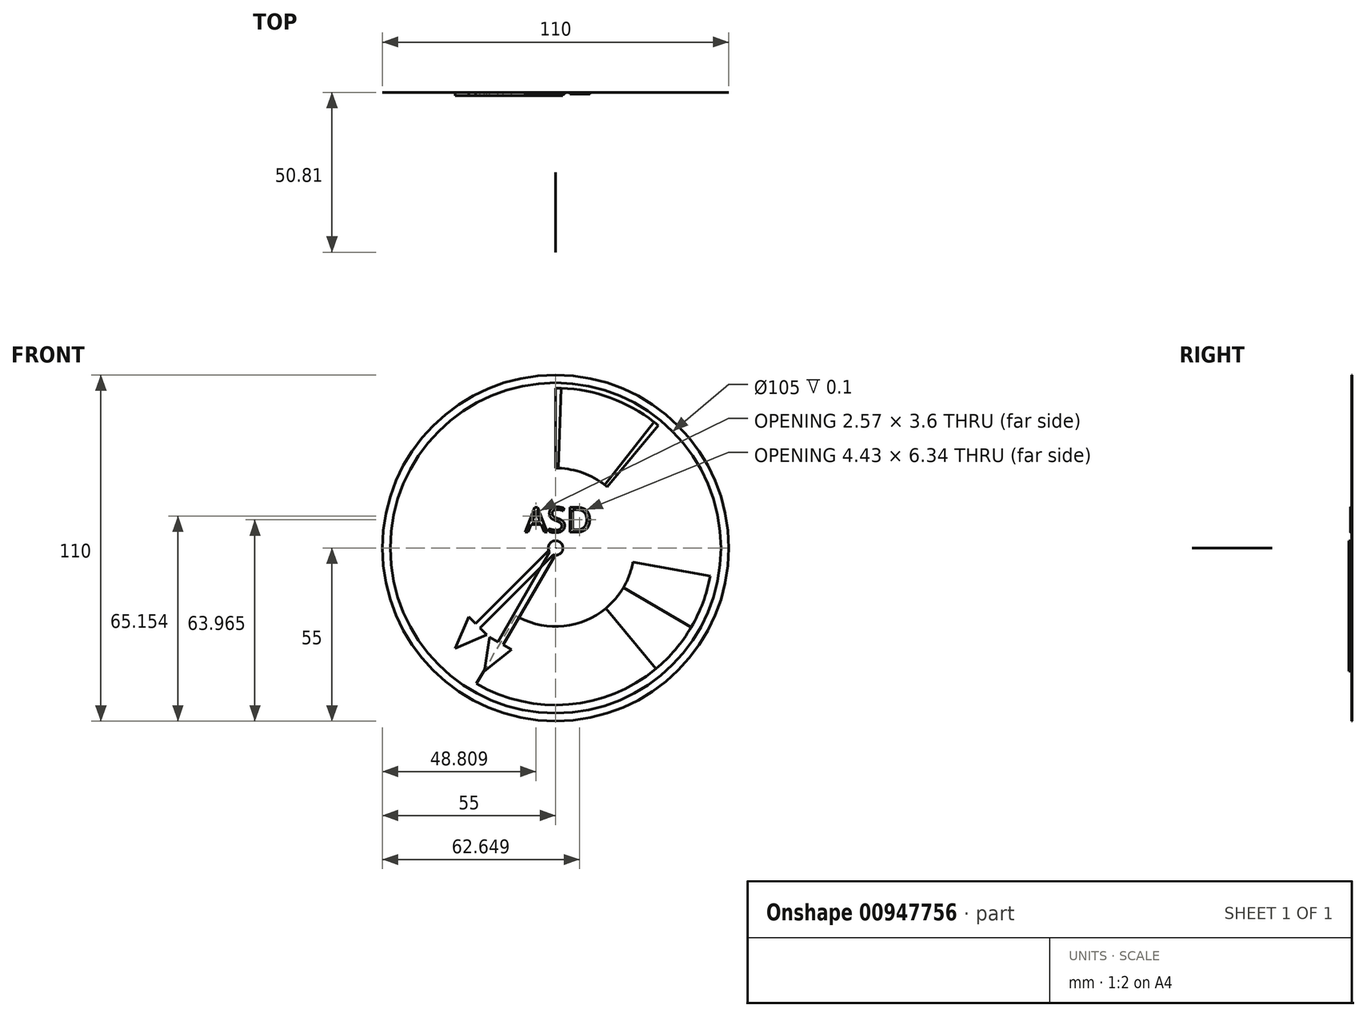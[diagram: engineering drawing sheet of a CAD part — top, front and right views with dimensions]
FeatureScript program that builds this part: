
annotation { "Feature Type Name" : "Feature", "Feature Type Description" : "" }
export const myFeature = defineFeature(function(context is Context, id is Id, definition is map)
    precondition{}
    {
        {
            var Q0;
            Q0=qCreatedBy(makeId("Right.planeOp"),FACE);
            var sketch = newSketch(context, id + "F0", { "sketchPlane" : qUnion([Q0])});
            skLineSegment(sketch, "E0", {"start": v(0, 0) * mm, "end": v(-116.06, 0) * mm, "construction": true});
            skSolve(sketch);
        }
        {
            var Q0;
            Q0=qCreatedBy(makeId("Right.planeOp"),FACE);
            var Q1;
            Q1=sQuery(id+"F0.wireOp",EDGE,"E0");
            cPlane(context, id + "F1", {"entities" : qUnion([Q0, Q1]), "cplaneType" : CPlaneType.LINE_ANGLE, "offset" : 25 * mm, "angle" : 135 * degree, "width" : 150 * mm, "height" : 150 * mm});
        }
        {
            var Q0;
            Q0=qCreatedBy(id+"F1.planeOp",FACE);
            var sketch = newSketch(context, id + "F2", { "sketchPlane" : qUnion([Q0])});
            skLineSegment(sketch, "E1.bottom", {"start": v(-25.4, 0) * mm, "end": v(-50.8, 0) * mm});
            skLineSegment(sketch, "E1.top", {"start": v(-25.4, 0) * mm, "end": v(-50.8, 0) * mm});
            skLineSegment(sketch, "E1.left", {"start": v(-25.4, 0) * mm, "end": v(-25.4, 0) * mm});
            skLineSegment(sketch, "E1.right", {"start": v(-50.8, 0) * mm, "end": v(-50.8, 0) * mm});
            skSolve(sketch);
        }
        {
            var Q0;
            Q0=qSketchRegion(id+"F2",true);
            var Q1;
            Q1=sQuery(id+"F0.wireOp",EDGE,"E0");
            revolve(context, id + "F3", {"surfaceOperationType" : NewSurfaceOperationType.NEW, "entities" : qUnion([Q0]), "axis" : qUnion([Q1]), "revolveType" : RevolveType.ONE_DIRECTION, "oppositeDirection" : true, "angle" : 135 * degree});
        }
        {
            var Q0;
            Q0=qCreatedBy(makeId("Right.planeOp"),FACE);
            var sketch = newSketch(context, id + "F4", { "sketchPlane" : qUnion([Q0])});
            skLineSegment(sketch, "E2.bottom", {"start": v(-0.01, 50.8) * mm, "end": v(0, 50.8) * mm});
            skLineSegment(sketch, "E2.top", {"start": v(0, 25.4) * mm, "end": v(0, 25.4) * mm});
            skLineSegment(sketch, "E2.left", {"start": v(-0.01, 50.8) * mm, "end": v(0, 25.4) * mm});
            skLineSegment(sketch, "E2.right", {"start": v(0, 50.8) * mm, "end": v(0, 25.4) * mm});
            skSolve(sketch);
        }
        {
            var Q0;
            Q0=qSketchRegion(id+"F4",true);
            var Q1;
            Q1=sQuery(id+"F0.wireOp",EDGE,"E0");
            revolve(context, id + "F5", {"surfaceOperationType" : NewSurfaceOperationType.NEW, "entities" : qUnion([Q0]), "axis" : qUnion([Q1]), "revolveType" : RevolveType.ONE_DIRECTION, "oppositeDirection" : true, "angle" : 2 * degree});
        }
        {
            var Q0;
            Q0=qCreatedBy(makeId("Right.planeOp"),FACE);
            var Q1;
            Q1=sQuery(id+"F0.wireOp",EDGE,"E0");
            cPlane(context, id + "F6", {"entities" : qUnion([Q0, Q1]), "cplaneType" : CPlaneType.LINE_ANGLE, "offset" : 25 * mm, "angle" : 2 * degree, "oppositeDirection" : true, "width" : 150 * mm, "height" : 150 * mm});
        }
        {
            var Q0;
            Q0=qCreatedBy(id+"F6.planeOp",FACE);
            var sketch = newSketch(context, id + "F7", { "sketchPlane" : qUnion([Q0])});
            skLineSegment(sketch, "E3.bottom", {"start": v(0, 50.8) * mm, "end": v(0, 50.8) * mm});
            skLineSegment(sketch, "E3.top", {"start": v(0, 25.4) * mm, "end": v(0, 25.4) * mm});
            skLineSegment(sketch, "E3.left", {"start": v(0, 50.8) * mm, "end": v(0, 25.4) * mm});
            skLineSegment(sketch, "E3.right", {"start": v(0, 50.8) * mm, "end": v(0, 25.4) * mm});
            skSolve(sketch);
        }
        {
            var Q0;
            Q0=qSketchRegion(id+"F7",true);
            var Q1;
            Q1=sQuery(id+"F0.wireOp",EDGE,"E0");
            revolve(context, id + "F8", {"surfaceOperationType" : NewSurfaceOperationType.NEW, "entities" : qUnion([Q0]), "axis" : qUnion([Q1]), "revolveType" : RevolveType.ONE_DIRECTION, "oppositeDirection" : true, "angle" : 36 * degree});
        }
        {
            var Q0;
            Q0=qCreatedBy(makeId("Front.planeOp"),FACE);
            var sketch = newSketch(context, id + "F9", { "sketchPlane" : qUnion([Q0])});
            skLineSegment(sketch, "E4.bottom", {"start": v(-0.77, -2.19) * mm, "end": v(-24.04, -25.46) * mm});
            skLineSegment(sketch, "E4.top", {"start": v(-2.19, -0.77) * mm, "end": v(-25.46, -24.04) * mm});
            skPoint(sketch, "E4.middle", {"position": v(0, 0) * mm});
            skLineSegment(sketch, "E5", {"start": v(0, 0) * mm, "end": v(0, 10.99) * mm, "construction": true});
            skPoint(sketch, "E6", {"position": v(-24.75, -24.75) * mm});
            skCircle(sketch, "E7", {"center": v(-24.75, -24.75) * mm, "radius": 10.19 * mm, "construction": true});
            skLineSegment(sketch, "E8", {"start": v(-24.04, -25.46) * mm, "end": v(-21.92, -27.58) * mm});
            skLineSegment(sketch, "E9", {"start": v(-25.46, -24.04) * mm, "end": v(-27.58, -21.92) * mm});
            skLineSegment(sketch, "E10", {"start": v(-24.75, -24.75) * mm, "end": v(-31.95, -31.95) * mm, "construction": true});
            skLineSegment(sketch, "E11", {"start": v(-31.95, -31.95) * mm, "end": v(-27.58, -21.92) * mm});
            skLineSegment(sketch, "E12", {"start": v(-21.92, -27.58) * mm, "end": v(-31.95, -31.95) * mm});
            skArc(sketch, "E13", {"start": v(-0.77, -2.19) * mm, "mid": v(1.64, 1.64) * mm, "end": v(-2.19, -0.77) * mm});
            skPoint(sketch, "E14.orphan", {"position": v(-0.7, 0.7) * mm});
            skPoint(sketch, "E15.end.orphan", {"position": v(0.7, -0.7) * mm});
            skSolve(sketch);
        }
        {
            var Q0;
            Q0=qSketchRegion(id+"F9",true);
            extrude(context, id + "F10", {"entities" : qUnion([Q0]), "depth" : 1 * mm, "offsetDistance" : 25 * mm});
        }
        {
            var Q0;
            Q0=qCreatedBy(makeId("Front.planeOp"),FACE);
            var sketch = newSketch(context, id + "F11", { "sketchPlane" : qUnion([Q0])});
            skCircle(sketch, "E16", {"center": v(0, 0) * mm, "radius": 52.5 * mm});
            skCircle(sketch, "E17", {"center": v(0, 0) * mm, "radius": 55 * mm});
            skSolve(sketch);
        }
        {
            var Q0;
            Q0=qSketchRegion(id+"F11",true);
            extrude(context, id + "F12", {"entities" : qUnion([Q0]), "depth" : .1 * mm, "offsetDistance" : 25 * mm});
        }
        {
            var Q0;
            Q0=qCreatedBy(makeId("Front.planeOp"),FACE);
            var sketch = newSketch(context, id + "F13", { "sketchPlane" : qUnion([Q0])});
            skPoint(sketch, "E18.middle", {"position": v(68.26, -76.77) * mm});
            skText(sketch, "E19", { "text": "SPEED", "fontName": "OpenSans-Bold.ttf"});
            skLineSegment(sketch, "E20", {"start": v(0, 0) * mm, "end": v(0, -24.7) * mm, "construction": true});
            const initialGuessF13  = {"E19": [-0.015, -0.03702, 1, 0, 0.007]};
            skSetInitialGuess(sketch, initialGuessF13);
            skSolve(sketch);
        }
        {
            var Q0;
            Q0 = qSketchRegion(id + "F13", true);
            extrude(context, id + "F14", {"entities" : qUnion([Q0]), "depth" : .1 * mm, "offsetDistance" : 25 * mm});
        }
        {
            var Q0;
            Q0=qCreatedBy(makeId("Front.planeOp"),FACE);
            var sketch = newSketch(context, id + "F15", { "sketchPlane" : qUnion([Q0])});
            skLineSegment(sketch, "E21", {"start": v(3.53, 25.15) * mm, "end": v(7.07, 50.3) * mm});
            skLineSegment(sketch, "E22", {"start": v(0, 0) * mm, "end": v(0, 18.46) * mm, "construction": true});
            skArc(sketch, "E23", {"start": v(3.53, 25.15) * mm, "mid": v(3.97, 25.09) * mm, "end": v(4.41, 25.01) * mm});
            skArc(sketch, "E24", {"start": v(7.07, 50.3) * mm, "mid": v(7.95, 50.17) * mm, "end": v(8.82, 50.03) * mm});
            skLineSegment(sketch, "E25", {"start": v(4.41, 25.01) * mm, "end": v(8.82, 50.03) * mm});
            skSolve(sketch);
        }
        {
            var Q0;
            Q0 = qSketchRegion(id + "F15", true);
            extrude(context, id + "F16", {"entities" : qUnion([Q0]), "depth" : .1 * mm, "offsetDistance" : 25 * mm});
        }
        {
            var Q0;
            Q0=makeQuery(id+"F16.opExtrude","SWEPT_BODY",BODY,{"disambiguationData":[OSD([sQuery(id+"F15.wireOp",EDGE,"E21"),sQuery(id+"F15.wireOp",EDGE,"E23"),sQuery(id+"F15.wireOp",EDGE,"E24"),sQuery(id+"F15.wireOp",EDGE,"E25")])]});
            var Q1;
            Q1=makeQuery(id+"F12.opExtrude","CAP_EDGE",EDGE,{"disambiguationData":[OSD([sQuery(id+"F11.wireOp",EDGE,"E16")])],"isStart":false});
            transform(context, id + "F17", {"entities" : qUnion([Q0]), "transformType" : TransformType.ROTATION, "transformAxis" : qUnion([Q1]), "angle" : 30 * degree, "oppositeDirection" : true, "makeCopy" : false});
        }
        {
            var Q0;
            Q0=makeQuery(id+"F14.opExtrude","SWEPT_BODY",BODY,{"disambiguationData":[OSD([sQuery(id+"F13.wireOp",EDGE,"E19.sketch_text.stroke-0"),sQuery(id+"F13.wireOp",EDGE,"E19.sketch_text.stroke-1"),sQuery(id+"F13.wireOp",EDGE,"E19.sketch_text.stroke-2"),sQuery(id+"F13.wireOp",EDGE,"E19.sketch_text.stroke-3"),sQuery(id+"F13.wireOp",EDGE,"E19.sketch_text.stroke-4"),sQuery(id+"F13.wireOp",EDGE,"E19.sketch_text.stroke-5"),sQuery(id+"F13.wireOp",EDGE,"E19.sketch_text.stroke-6"),sQuery(id+"F13.wireOp",EDGE,"E19.sketch_text.stroke-7"),sQuery(id+"F13.wireOp",EDGE,"E19.sketch_text.stroke-8"),sQuery(id+"F13.wireOp",EDGE,"E19.sketch_text.stroke-9"),sQuery(id+"F13.wireOp",EDGE,"E19.sketch_text.stroke-10"),sQuery(id+"F13.wireOp",EDGE,"E19.sketch_text.stroke-11"),sQuery(id+"F13.wireOp",EDGE,"E19.sketch_text.stroke-12"),sQuery(id+"F13.wireOp",EDGE,"E19.sketch_text.stroke-13"),sQuery(id+"F13.wireOp",EDGE,"E19.sketch_text.stroke-14"),sQuery(id+"F13.wireOp",EDGE,"E19.sketch_text.stroke-15"),sQuery(id+"F13.wireOp",EDGE,"E19.sketch_text.stroke-16"),sQuery(id+"F13.wireOp",EDGE,"E19.sketch_text.stroke-17"),sQuery(id+"F13.wireOp",EDGE,"E19.sketch_text.stroke-18"),sQuery(id+"F13.wireOp",EDGE,"E19.sketch_text.stroke-19"),sQuery(id+"F13.wireOp",EDGE,"E19.sketch_text.stroke-20"),sQuery(id+"F13.wireOp",EDGE,"E19.sketch_text.stroke-21"),sQuery(id+"F13.wireOp",EDGE,"E19.sketch_text.stroke-22"),sQuery(id+"F13.wireOp",EDGE,"E19.sketch_text.stroke-23"),sQuery(id+"F13.wireOp",EDGE,"E19.sketch_text.stroke-24"),sQuery(id+"F13.wireOp",EDGE,"E19.sketch_text.stroke-25"),sQuery(id+"F13.wireOp",EDGE,"E19.sketch_text.stroke-26"),sQuery(id+"F13.wireOp",EDGE,"E19.sketch_text.stroke-27")])]});
            var Q1;
            Q1=makeQuery(id+"F14.opExtrude","SWEPT_BODY",BODY,{"disambiguationData":[OSD([sQuery(id+"F13.wireOp",EDGE,"E19.sketch_text.stroke-28"),sQuery(id+"F13.wireOp",EDGE,"E19.sketch_text.stroke-29"),sQuery(id+"F13.wireOp",EDGE,"E19.sketch_text.stroke-30"),sQuery(id+"F13.wireOp",EDGE,"E19.sketch_text.stroke-31"),sQuery(id+"F13.wireOp",EDGE,"E19.sketch_text.stroke-32"),sQuery(id+"F13.wireOp",EDGE,"E19.sketch_text.stroke-33"),sQuery(id+"F13.wireOp",EDGE,"E19.sketch_text.stroke-34"),sQuery(id+"F13.wireOp",EDGE,"E19.sketch_text.stroke-35"),sQuery(id+"F13.wireOp",EDGE,"E19.sketch_text.stroke-36"),sQuery(id+"F13.wireOp",EDGE,"E19.sketch_text.stroke-37"),sQuery(id+"F13.wireOp",EDGE,"E19.sketch_text.stroke-38"),sQuery(id+"F13.wireOp",EDGE,"E19.sketch_text.stroke-39"),sQuery(id+"F13.wireOp",EDGE,"E19.sketch_text.stroke-40"),sQuery(id+"F13.wireOp",EDGE,"E19.sketch_text.stroke-41"),sQuery(id+"F13.wireOp",EDGE,"E19.sketch_text.stroke-42"),sQuery(id+"F13.wireOp",EDGE,"E19.sketch_text.stroke-43")])]});
            var Q2;
            Q2=makeQuery(id+"F14.opExtrude","SWEPT_BODY",BODY,{"disambiguationData":[OSD([sQuery(id+"F13.wireOp",EDGE,"E19.sketch_text.stroke-44"),sQuery(id+"F13.wireOp",EDGE,"E19.sketch_text.stroke-45"),sQuery(id+"F13.wireOp",EDGE,"E19.sketch_text.stroke-46"),sQuery(id+"F13.wireOp",EDGE,"E19.sketch_text.stroke-47"),sQuery(id+"F13.wireOp",EDGE,"E19.sketch_text.stroke-48"),sQuery(id+"F13.wireOp",EDGE,"E19.sketch_text.stroke-49"),sQuery(id+"F13.wireOp",EDGE,"E19.sketch_text.stroke-50"),sQuery(id+"F13.wireOp",EDGE,"E19.sketch_text.stroke-51"),sQuery(id+"F13.wireOp",EDGE,"E19.sketch_text.stroke-52"),sQuery(id+"F13.wireOp",EDGE,"E19.sketch_text.stroke-53"),sQuery(id+"F13.wireOp",EDGE,"E19.sketch_text.stroke-54"),sQuery(id+"F13.wireOp",EDGE,"E19.sketch_text.stroke-55")])]});
            var Q3;
            Q3=makeQuery(id+"F14.opExtrude","SWEPT_BODY",BODY,{"disambiguationData":[OSD([sQuery(id+"F13.wireOp",EDGE,"E19.sketch_text.stroke-56"),sQuery(id+"F13.wireOp",EDGE,"E19.sketch_text.stroke-57"),sQuery(id+"F13.wireOp",EDGE,"E19.sketch_text.stroke-58"),sQuery(id+"F13.wireOp",EDGE,"E19.sketch_text.stroke-59"),sQuery(id+"F13.wireOp",EDGE,"E19.sketch_text.stroke-60"),sQuery(id+"F13.wireOp",EDGE,"E19.sketch_text.stroke-61"),sQuery(id+"F13.wireOp",EDGE,"E19.sketch_text.stroke-62"),sQuery(id+"F13.wireOp",EDGE,"E19.sketch_text.stroke-63"),sQuery(id+"F13.wireOp",EDGE,"E19.sketch_text.stroke-64"),sQuery(id+"F13.wireOp",EDGE,"E19.sketch_text.stroke-65"),sQuery(id+"F13.wireOp",EDGE,"E19.sketch_text.stroke-66"),sQuery(id+"F13.wireOp",EDGE,"E19.sketch_text.stroke-67")])]});
            var Q4;
            Q4=makeQuery(id+"F14.opExtrude","SWEPT_BODY",BODY,{"disambiguationData":[OSD([sQuery(id+"F13.wireOp",EDGE,"E19.sketch_text.stroke-68"),sQuery(id+"F13.wireOp",EDGE,"E19.sketch_text.stroke-69"),sQuery(id+"F13.wireOp",EDGE,"E19.sketch_text.stroke-70"),sQuery(id+"F13.wireOp",EDGE,"E19.sketch_text.stroke-71"),sQuery(id+"F13.wireOp",EDGE,"E19.sketch_text.stroke-72"),sQuery(id+"F13.wireOp",EDGE,"E19.sketch_text.stroke-73"),sQuery(id+"F13.wireOp",EDGE,"E19.sketch_text.stroke-74"),sQuery(id+"F13.wireOp",EDGE,"E19.sketch_text.stroke-75"),sQuery(id+"F13.wireOp",EDGE,"E19.sketch_text.stroke-76"),sQuery(id+"F13.wireOp",EDGE,"E19.sketch_text.stroke-77"),sQuery(id+"F13.wireOp",EDGE,"E19.sketch_text.stroke-78"),sQuery(id+"F13.wireOp",EDGE,"E19.sketch_text.stroke-79")])]});
            deleteBodies(context, id + "F18", {"entities" : qUnion([Q0, Q1, Q2, Q3, Q4])});
        }
        {
            var Q0;
            Q0=qCreatedBy(makeId("Front.planeOp"),FACE);
            var sketch = newSketch(context, id + "F19", { "sketchPlane" : qUnion([Q0])});
            skText(sketch, "E26", { "text": "     19\nKts/Sec", "fontName": "OpenSans-Regular.ttf"});
            const initialGuessF19  = {"E26": [0.00712, -0.01436, 1, 0, 0.007]};
            skSetInitialGuess(sketch, initialGuessF19);
            skSolve(sketch);
        }
        {
            var Q0;
            Q0 = qSketchRegion(id + "F19", true);
            extrude(context, id + "F20", {"entities" : qUnion([Q0]), "depth" : 0.5 * mm, "offsetDistance" : 25 * mm});
        }
        {
            var Q0;
            Q0=makeQuery(id+"F20.opExtrude","SWEPT_BODY",BODY,{"disambiguationData":[OSD([sQuery(id+"F19.wireOp",EDGE,"E26.sketch_text.stroke-139"),sQuery(id+"F19.wireOp",EDGE,"E26.sketch_text.stroke-140"),sQuery(id+"F19.wireOp",EDGE,"E26.sketch_text.stroke-141"),sQuery(id+"F19.wireOp",EDGE,"E26.sketch_text.stroke-142"),sQuery(id+"F19.wireOp",EDGE,"E26.sketch_text.stroke-143"),sQuery(id+"F19.wireOp",EDGE,"E26.sketch_text.stroke-144"),sQuery(id+"F19.wireOp",EDGE,"E26.sketch_text.stroke-145"),sQuery(id+"F19.wireOp",EDGE,"E26.sketch_text.stroke-146"),sQuery(id+"F19.wireOp",EDGE,"E26.sketch_text.stroke-147"),sQuery(id+"F19.wireOp",EDGE,"E26.sketch_text.stroke-148"),sQuery(id+"F19.wireOp",EDGE,"E26.sketch_text.stroke-149"),sQuery(id+"F19.wireOp",EDGE,"E26.sketch_text.stroke-150"),sQuery(id+"F19.wireOp",EDGE,"E26.sketch_text.stroke-151"),sQuery(id+"F19.wireOp",EDGE,"E26.sketch_text.stroke-152"),sQuery(id+"F19.wireOp",EDGE,"E26.sketch_text.stroke-153")])]});
            var Q1;
            Q1=makeQuery(id+"F20.opExtrude","SWEPT_BODY",BODY,{"disambiguationData":[OSD([sQuery(id+"F19.wireOp",EDGE,"E26.sketch_text.stroke-120"),sQuery(id+"F19.wireOp",EDGE,"E26.sketch_text.stroke-121"),sQuery(id+"F19.wireOp",EDGE,"E26.sketch_text.stroke-122"),sQuery(id+"F19.wireOp",EDGE,"E26.sketch_text.stroke-123"),sQuery(id+"F19.wireOp",EDGE,"E26.sketch_text.stroke-124"),sQuery(id+"F19.wireOp",EDGE,"E26.sketch_text.stroke-125"),sQuery(id+"F19.wireOp",EDGE,"E26.sketch_text.stroke-126"),sQuery(id+"F19.wireOp",EDGE,"E26.sketch_text.stroke-127"),sQuery(id+"F19.wireOp",EDGE,"E26.sketch_text.stroke-128"),sQuery(id+"F19.wireOp",EDGE,"E26.sketch_text.stroke-129"),sQuery(id+"F19.wireOp",EDGE,"E26.sketch_text.stroke-130"),sQuery(id+"F19.wireOp",EDGE,"E26.sketch_text.stroke-131"),sQuery(id+"F19.wireOp",EDGE,"E26.sketch_text.stroke-132"),sQuery(id+"F19.wireOp",EDGE,"E26.sketch_text.stroke-133"),sQuery(id+"F19.wireOp",EDGE,"E26.sketch_text.stroke-134"),sQuery(id+"F19.wireOp",EDGE,"E26.sketch_text.stroke-135"),sQuery(id+"F19.wireOp",EDGE,"E26.sketch_text.stroke-136"),sQuery(id+"F19.wireOp",EDGE,"E26.sketch_text.stroke-137"),sQuery(id+"F19.wireOp",EDGE,"E26.sketch_text.stroke-138")])]});
            var Q2;
            Q2=makeQuery(id+"F20.opExtrude","SWEPT_BODY",BODY,{"disambiguationData":[OSD([sQuery(id+"F19.wireOp",EDGE,"E26.sketch_text.stroke-95"),sQuery(id+"F19.wireOp",EDGE,"E26.sketch_text.stroke-96"),sQuery(id+"F19.wireOp",EDGE,"E26.sketch_text.stroke-97"),sQuery(id+"F19.wireOp",EDGE,"E26.sketch_text.stroke-98"),sQuery(id+"F19.wireOp",EDGE,"E26.sketch_text.stroke-99"),sQuery(id+"F19.wireOp",EDGE,"E26.sketch_text.stroke-100"),sQuery(id+"F19.wireOp",EDGE,"E26.sketch_text.stroke-101"),sQuery(id+"F19.wireOp",EDGE,"E26.sketch_text.stroke-102"),sQuery(id+"F19.wireOp",EDGE,"E26.sketch_text.stroke-103"),sQuery(id+"F19.wireOp",EDGE,"E26.sketch_text.stroke-104"),sQuery(id+"F19.wireOp",EDGE,"E26.sketch_text.stroke-105"),sQuery(id+"F19.wireOp",EDGE,"E26.sketch_text.stroke-106"),sQuery(id+"F19.wireOp",EDGE,"E26.sketch_text.stroke-107"),sQuery(id+"F19.wireOp",EDGE,"E26.sketch_text.stroke-108"),sQuery(id+"F19.wireOp",EDGE,"E26.sketch_text.stroke-109"),sQuery(id+"F19.wireOp",EDGE,"E26.sketch_text.stroke-110"),sQuery(id+"F19.wireOp",EDGE,"E26.sketch_text.stroke-111"),sQuery(id+"F19.wireOp",EDGE,"E26.sketch_text.stroke-112"),sQuery(id+"F19.wireOp",EDGE,"E26.sketch_text.stroke-113"),sQuery(id+"F19.wireOp",EDGE,"E26.sketch_text.stroke-114"),sQuery(id+"F19.wireOp",EDGE,"E26.sketch_text.stroke-115"),sQuery(id+"F19.wireOp",EDGE,"E26.sketch_text.stroke-116"),sQuery(id+"F19.wireOp",EDGE,"E26.sketch_text.stroke-117"),sQuery(id+"F19.wireOp",EDGE,"E26.sketch_text.stroke-118"),sQuery(id+"F19.wireOp",EDGE,"E26.sketch_text.stroke-119")])]});
            var Q3;
            Q3=makeQuery(id+"F20.opExtrude","SWEPT_BODY",BODY,{"disambiguationData":[OSD([sQuery(id+"F19.wireOp",EDGE,"E26.sketch_text.stroke-91"),sQuery(id+"F19.wireOp",EDGE,"E26.sketch_text.stroke-92"),sQuery(id+"F19.wireOp",EDGE,"E26.sketch_text.stroke-93"),sQuery(id+"F19.wireOp",EDGE,"E26.sketch_text.stroke-94")])]});
            var Q4;
            Q4=makeQuery(id+"F20.opExtrude","SWEPT_BODY",BODY,{"disambiguationData":[OSD([sQuery(id+"F19.wireOp",EDGE,"E26.sketch_text.stroke-66"),sQuery(id+"F19.wireOp",EDGE,"E26.sketch_text.stroke-67"),sQuery(id+"F19.wireOp",EDGE,"E26.sketch_text.stroke-68"),sQuery(id+"F19.wireOp",EDGE,"E26.sketch_text.stroke-69"),sQuery(id+"F19.wireOp",EDGE,"E26.sketch_text.stroke-70"),sQuery(id+"F19.wireOp",EDGE,"E26.sketch_text.stroke-71"),sQuery(id+"F19.wireOp",EDGE,"E26.sketch_text.stroke-72"),sQuery(id+"F19.wireOp",EDGE,"E26.sketch_text.stroke-73"),sQuery(id+"F19.wireOp",EDGE,"E26.sketch_text.stroke-74"),sQuery(id+"F19.wireOp",EDGE,"E26.sketch_text.stroke-75"),sQuery(id+"F19.wireOp",EDGE,"E26.sketch_text.stroke-76"),sQuery(id+"F19.wireOp",EDGE,"E26.sketch_text.stroke-77"),sQuery(id+"F19.wireOp",EDGE,"E26.sketch_text.stroke-78"),sQuery(id+"F19.wireOp",EDGE,"E26.sketch_text.stroke-79"),sQuery(id+"F19.wireOp",EDGE,"E26.sketch_text.stroke-80"),sQuery(id+"F19.wireOp",EDGE,"E26.sketch_text.stroke-81"),sQuery(id+"F19.wireOp",EDGE,"E26.sketch_text.stroke-82"),sQuery(id+"F19.wireOp",EDGE,"E26.sketch_text.stroke-83"),sQuery(id+"F19.wireOp",EDGE,"E26.sketch_text.stroke-84"),sQuery(id+"F19.wireOp",EDGE,"E26.sketch_text.stroke-85"),sQuery(id+"F19.wireOp",EDGE,"E26.sketch_text.stroke-86"),sQuery(id+"F19.wireOp",EDGE,"E26.sketch_text.stroke-87"),sQuery(id+"F19.wireOp",EDGE,"E26.sketch_text.stroke-88"),sQuery(id+"F19.wireOp",EDGE,"E26.sketch_text.stroke-89"),sQuery(id+"F19.wireOp",EDGE,"E26.sketch_text.stroke-90")])]});
            var Q5;
            Q5=makeQuery(id+"F20.opExtrude","SWEPT_BODY",BODY,{"disambiguationData":[OSD([sQuery(id+"F19.wireOp",EDGE,"E26.sketch_text.stroke-47"),sQuery(id+"F19.wireOp",EDGE,"E26.sketch_text.stroke-48"),sQuery(id+"F19.wireOp",EDGE,"E26.sketch_text.stroke-49"),sQuery(id+"F19.wireOp",EDGE,"E26.sketch_text.stroke-50"),sQuery(id+"F19.wireOp",EDGE,"E26.sketch_text.stroke-51"),sQuery(id+"F19.wireOp",EDGE,"E26.sketch_text.stroke-52"),sQuery(id+"F19.wireOp",EDGE,"E26.sketch_text.stroke-53"),sQuery(id+"F19.wireOp",EDGE,"E26.sketch_text.stroke-54"),sQuery(id+"F19.wireOp",EDGE,"E26.sketch_text.stroke-55"),sQuery(id+"F19.wireOp",EDGE,"E26.sketch_text.stroke-56"),sQuery(id+"F19.wireOp",EDGE,"E26.sketch_text.stroke-57"),sQuery(id+"F19.wireOp",EDGE,"E26.sketch_text.stroke-58"),sQuery(id+"F19.wireOp",EDGE,"E26.sketch_text.stroke-59"),sQuery(id+"F19.wireOp",EDGE,"E26.sketch_text.stroke-60"),sQuery(id+"F19.wireOp",EDGE,"E26.sketch_text.stroke-61"),sQuery(id+"F19.wireOp",EDGE,"E26.sketch_text.stroke-62"),sQuery(id+"F19.wireOp",EDGE,"E26.sketch_text.stroke-63"),sQuery(id+"F19.wireOp",EDGE,"E26.sketch_text.stroke-64"),sQuery(id+"F19.wireOp",EDGE,"E26.sketch_text.stroke-65")])]});
            var Q6;
            Q6=makeQuery(id+"F20.opExtrude","SWEPT_BODY",BODY,{"disambiguationData":[OSD([sQuery(id+"F19.wireOp",EDGE,"E26.sketch_text.stroke-35"),sQuery(id+"F19.wireOp",EDGE,"E26.sketch_text.stroke-36"),sQuery(id+"F19.wireOp",EDGE,"E26.sketch_text.stroke-37"),sQuery(id+"F19.wireOp",EDGE,"E26.sketch_text.stroke-38"),sQuery(id+"F19.wireOp",EDGE,"E26.sketch_text.stroke-39"),sQuery(id+"F19.wireOp",EDGE,"E26.sketch_text.stroke-40"),sQuery(id+"F19.wireOp",EDGE,"E26.sketch_text.stroke-41"),sQuery(id+"F19.wireOp",EDGE,"E26.sketch_text.stroke-42"),sQuery(id+"F19.wireOp",EDGE,"E26.sketch_text.stroke-43"),sQuery(id+"F19.wireOp",EDGE,"E26.sketch_text.stroke-44"),sQuery(id+"F19.wireOp",EDGE,"E26.sketch_text.stroke-45"),sQuery(id+"F19.wireOp",EDGE,"E26.sketch_text.stroke-46")])]});
            var Q7;
            Q7=makeQuery(id+"F20.opExtrude","SWEPT_BODY",BODY,{"disambiguationData":[OSD([sQuery(id+"F19.wireOp",EDGE,"E26.sketch_text.stroke-9"),sQuery(id+"F19.wireOp",EDGE,"E26.sketch_text.stroke-10"),sQuery(id+"F19.wireOp",EDGE,"E26.sketch_text.stroke-11"),sQuery(id+"F19.wireOp",EDGE,"E26.sketch_text.stroke-12"),sQuery(id+"F19.wireOp",EDGE,"E26.sketch_text.stroke-13"),sQuery(id+"F19.wireOp",EDGE,"E26.sketch_text.stroke-14"),sQuery(id+"F19.wireOp",EDGE,"E26.sketch_text.stroke-15"),sQuery(id+"F19.wireOp",EDGE,"E26.sketch_text.stroke-16"),sQuery(id+"F19.wireOp",EDGE,"E26.sketch_text.stroke-17"),sQuery(id+"F19.wireOp",EDGE,"E26.sketch_text.stroke-18"),sQuery(id+"F19.wireOp",EDGE,"E26.sketch_text.stroke-19"),sQuery(id+"F19.wireOp",EDGE,"E26.sketch_text.stroke-20"),sQuery(id+"F19.wireOp",EDGE,"E26.sketch_text.stroke-21"),sQuery(id+"F19.wireOp",EDGE,"E26.sketch_text.stroke-22"),sQuery(id+"F19.wireOp",EDGE,"E26.sketch_text.stroke-23"),sQuery(id+"F19.wireOp",EDGE,"E26.sketch_text.stroke-24"),sQuery(id+"F19.wireOp",EDGE,"E26.sketch_text.stroke-25"),sQuery(id+"F19.wireOp",EDGE,"E26.sketch_text.stroke-26"),sQuery(id+"F19.wireOp",EDGE,"E26.sketch_text.stroke-27"),sQuery(id+"F19.wireOp",EDGE,"E26.sketch_text.stroke-28"),sQuery(id+"F19.wireOp",EDGE,"E26.sketch_text.stroke-29"),sQuery(id+"F19.wireOp",EDGE,"E26.sketch_text.stroke-30"),sQuery(id+"F19.wireOp",EDGE,"E26.sketch_text.stroke-31"),sQuery(id+"F19.wireOp",EDGE,"E26.sketch_text.stroke-32"),sQuery(id+"F19.wireOp",EDGE,"E26.sketch_text.stroke-33"),sQuery(id+"F19.wireOp",EDGE,"E26.sketch_text.stroke-34")])]});
            var Q8;
            Q8=makeQuery(id+"F20.opExtrude","SWEPT_BODY",BODY,{"disambiguationData":[OSD([sQuery(id+"F19.wireOp",EDGE,"E26.sketch_text.stroke-0"),sQuery(id+"F19.wireOp",EDGE,"E26.sketch_text.stroke-1"),sQuery(id+"F19.wireOp",EDGE,"E26.sketch_text.stroke-2"),sQuery(id+"F19.wireOp",EDGE,"E26.sketch_text.stroke-3"),sQuery(id+"F19.wireOp",EDGE,"E26.sketch_text.stroke-4"),sQuery(id+"F19.wireOp",EDGE,"E26.sketch_text.stroke-5"),sQuery(id+"F19.wireOp",EDGE,"E26.sketch_text.stroke-6"),sQuery(id+"F19.wireOp",EDGE,"E26.sketch_text.stroke-7"),sQuery(id+"F19.wireOp",EDGE,"E26.sketch_text.stroke-8")])]});
            deleteBodies(context, id + "F21", {"entities" : qUnion([Q0, Q1, Q2, Q3, Q4, Q5, Q6, Q7, Q8])});
        }
        {
            var Q0;
            Q0=qCreatedBy(makeId("Front.planeOp"),FACE);
            var sketch = newSketch(context, id + "F22", { "sketchPlane" : qUnion([Q0])});
            skLineSegment(sketch, "E27", {"start": v(0, 0) * mm, "end": v(-25.14, -43.08) * mm, "construction": true});
            skLineSegment(sketch, "E28", {"start": v(-25.14, -43.08) * mm, "end": v(-12.57, -21.54) * mm});
            skSolve(sketch);
        }
        {
            var Q0;
            Q0=sQuery(id+"F22.wireOp",EDGE,"E28");
            cPlane(context, id + "F23", {"entities" : qUnion([Q0]), "cplaneType" : CPlaneType.LINE_ANGLE, "offset" : 25 * mm, "angle" : 0 * degree, "width" : 150 * mm, "height" : 150 * mm});
        }
        {
            var Q0;
            Q0=qCreatedBy(id+"F23.planeOp",FACE);
            var sketch = newSketch(context, id + "F24", { "sketchPlane" : qUnion([Q0])});
            skLineSegment(sketch, "E29.bottom", {"start": v(0, -24.94) * mm, "end": v(0.01, -24.94) * mm});
            skLineSegment(sketch, "E29.top", {"start": v(0, -49.88) * mm, "end": v(0.01, -49.88) * mm});
            skLineSegment(sketch, "E29.left", {"start": v(0, -24.94) * mm, "end": v(0, -49.88) * mm});
            skLineSegment(sketch, "E29.right", {"start": v(0.01, -24.94) * mm, "end": v(0.01, -49.88) * mm});
            skSolve(sketch);
        }
        {
            var Q0;
            Q0 = qSketchRegion(id + "F24", true);
            var Q1;
            Q1=makeQuery(id+"F12.opExtrude","CAP_EDGE",EDGE,{"disambiguationData":[OSD([sQuery(id+"F11.wireOp",EDGE,"E16")])],"isStart":false});
            revolve(context, id + "F25", {"surfaceOperationType" : NewSurfaceOperationType.NEW, "entities" : qUnion([Q0]), "axis" : qUnion([Q1]), "revolveType" : RevolveType.ONE_DIRECTION, "angle" : 70 * degree});
        }
        {
            var Q0;
            Q0 = qSketchRegion(id + "F24", true);
            var Q1;
            Q1=makeQuery(id+"F12.opExtrude","CAP_EDGE",EDGE,{"disambiguationData":[OSD([sQuery(id+"F11.wireOp",EDGE,"E16")])],"isStart":false});
            revolve(context, id + "F26", {"operationType" : NewBodyOperationType.ADD, "surfaceOperationType" : NewSurfaceOperationType.NEW, "entities" : qUnion([Q0]), "axis" : qUnion([Q1]), "revolveType" : RevolveType.ONE_DIRECTION, "angle" : 10 * degree});
        }
        {
            var Q0;
            Q0 = qSketchRegion(id + "F24", true);
            var Q1;
            Q1=makeQuery(id+"F12.opExtrude","CAP_EDGE",EDGE,{"disambiguationData":[OSD([sQuery(id+"F11.wireOp",EDGE,"E17")])],"isStart":false});
            revolve(context, id + "F27", {"surfaceOperationType" : NewSurfaceOperationType.NEW, "entities" : qUnion([Q0]), "axis" : qUnion([Q1]), "revolveType" : RevolveType.ONE_DIRECTION, "angle" : 20 * degree});
        }
        {
            var Q0;
            Q0=makeQuery(id+"F27.opRevolve","SWEPT_BODY",BODY,{"disambiguationData":[OSD([sQuery(id+"F24.wireOp",EDGE,"E29.bottom"),sQuery(id+"F24.wireOp",EDGE,"E29.top"),sQuery(id+"F24.wireOp",EDGE,"E29.left"),sQuery(id+"F24.wireOp",EDGE,"E29.right")])]});
            var Q1;
            Q1=makeQuery(id+"F12.opExtrude","CAP_EDGE",EDGE,{"disambiguationData":[OSD([sQuery(id+"F11.wireOp",EDGE,"E16")])],"isStart":false});
            transform(context, id + "F28", {"entities" : qUnion([Q0]), "transformType" : TransformType.ROTATION, "transformAxis" : qUnion([Q1]), "angle" : 90 * degree, "makeCopy" : false});
        }
        {
            var Q0;
            Q0 = qSketchRegion(id + "F24", true);
            var Q1;
            Q1=makeQuery(id+"F12.opExtrude","CAP_EDGE",EDGE,{"disambiguationData":[OSD([sQuery(id+"F11.wireOp",EDGE,"E16")])],"isStart":false});
            revolve(context, id + "F29", {"operationType" : NewBodyOperationType.ADD, "surfaceOperationType" : NewSurfaceOperationType.NEW, "entities" : qUnion([Q0]), "axis" : qUnion([Q1]), "revolveType" : RevolveType.ONE_DIRECTION, "angle" : 15 * degree});
        }
        {
            var Q0;
            Q0 = qSketchRegion(id + "F24", true);
            var Q1;
            Q1=makeQuery(id+"F12.opExtrude","CAP_EDGE",EDGE,{"disambiguationData":[OSD([sQuery(id+"F11.wireOp",EDGE,"E17")])],"isStart":false});
            revolve(context, id + "F30", {"surfaceOperationType" : NewSurfaceOperationType.NEW, "entities" : qUnion([Q0]), "axis" : qUnion([Q1]), "revolveType" : RevolveType.ONE_DIRECTION, "angle" : 20 * degree});
        }
        {
            var Q0;
            Q0=makeQuery(id+"F30.opRevolve","SWEPT_BODY",BODY,{"disambiguationData":[OSD([sQuery(id+"F24.wireOp",EDGE,"E29.bottom"),sQuery(id+"F24.wireOp",EDGE,"E29.top"),sQuery(id+"F24.wireOp",EDGE,"E29.left"),sQuery(id+"F24.wireOp",EDGE,"E29.right")])]});
            var Q1;
            Q1=makeQuery(id+"F12.opExtrude","CAP_EDGE",EDGE,{"disambiguationData":[OSD([sQuery(id+"F11.wireOp",EDGE,"E17")])],"isStart":false});
            transform(context, id + "F31", {"entities" : qUnion([Q0]), "transformType" : TransformType.ROTATION, "transformAxis" : qUnion([Q1]), "angle" : 70 * degree, "makeCopy" : false});
        }
        {
            var Q0;
            Q0=makeQuery(id+"F10.opExtrude","SWEPT_BODY",BODY,{"disambiguationData":[OSD([sQuery(id+"F9.wireOp",EDGE,"E4.bottom"),sQuery(id+"F9.wireOp",EDGE,"E4.top"),sQuery(id+"F9.wireOp",EDGE,"E8"),sQuery(id+"F9.wireOp",EDGE,"E9"),sQuery(id+"F9.wireOp",EDGE,"E11"),sQuery(id+"F9.wireOp",EDGE,"E12"),sQuery(id+"F9.wireOp",EDGE,"E13")])]});
            transform(context, id + "F32", {"entities" : qUnion([Q0]), "transformType" : TransformType.TRANSLATION_3D, "dx" : 0 * mm, "dy" : 0 * mm, "dz" : 0 * mm, "makeCopy" : true});
        }
        {
            var Q0;
            Q0=makeQuery(id+"F32.opPattern","COPY",BODY,{"derivedFrom":makeQuery(id+"F10.opExtrude","SWEPT_BODY",BODY,{"disambiguationData":[OSD([sQuery(id+"F9.wireOp",EDGE,"E4.bottom"),sQuery(id+"F9.wireOp",EDGE,"E4.top"),sQuery(id+"F9.wireOp",EDGE,"E8"),sQuery(id+"F9.wireOp",EDGE,"E9"),sQuery(id+"F9.wireOp",EDGE,"E11"),sQuery(id+"F9.wireOp",EDGE,"E12"),sQuery(id+"F9.wireOp",EDGE,"E13")])]}),"instanceName":"1"});
            var Q1;
            Q1=makeQuery(id+"F12.opExtrude","CAP_EDGE",EDGE,{"disambiguationData":[OSD([sQuery(id+"F11.wireOp",EDGE,"E17")])],"isStart":false});
            transform(context, id + "F33", {"entities" : qUnion([Q0]), "transformType" : TransformType.ROTATION, "transformAxis" : qUnion([Q1]), "angle" : 15 * degree, "makeCopy" : false});
        }
        {
            var Q0;
            Q0=qCreatedBy(makeId("Front.planeOp"),FACE);
            var sketch = newSketch(context, id + "F34", { "sketchPlane" : qUnion([Q0])});
            skLineSegment(sketch, "E30", {"start": v(0, 0) * mm, "end": v(-42.47, -42.38) * mm, "construction": true});
            skSolve(sketch);
        }
        {
            var Q0;
            Q0=sQuery(id+"F34.wireOp",EDGE,"E30");
            cPlane(context, id + "F35", {"entities" : qUnion([Q0]), "cplaneType" : CPlaneType.LINE_ANGLE, "offset" : 25 * mm, "angle" : 90 * degree, "width" : 150 * mm, "height" : 150 * mm});
        }
        {
            var Q0;
            Q0=qCreatedBy(makeId("Front.planeOp"),FACE);
            var sketch = newSketch(context, id + "F36", { "sketchPlane" : qUnion([Q0])});
            skLineSegment(sketch, "E31", {"start": v(0, 0) * mm, "end": v(-30.23, -51.83) * mm, "construction": true});
            skSolve(sketch);
        }
        {
            var Q0;
            Q0=sQuery(id+"F36.wireOp",EDGE,"E31");
            cPlane(context, id + "F37", {"entities" : qUnion([Q0]), "cplaneType" : CPlaneType.LINE_ANGLE, "offset" : 25 * mm, "angle" : 0 * degree, "width" : 150 * mm, "height" : 150 * mm});
        }
        {
            var Q0;
            Q0=qCreatedBy(makeId("Front.planeOp"),FACE);
            var sketch = newSketch(context, id + "F38", { "sketchPlane" : qUnion([Q0])});
            skText(sketch, "E32", { "text": "ASD", "fontName": "OpenSans-Regular.ttf"});
            const initialGuessF38  = {"E32": [-0.00971, 0.005, 1, 0, 0.008]};
            skSetInitialGuess(sketch, initialGuessF38);
            skSolve(sketch);
        }
        {
            var Q0;
            Q0 = qSketchRegion(id + "F38", true);
            extrude(context, id + "F39", {"entities" : qUnion([Q0]), "depth" : 0.5 * mm, "offsetDistance" : 25 * mm});
        }
    });
